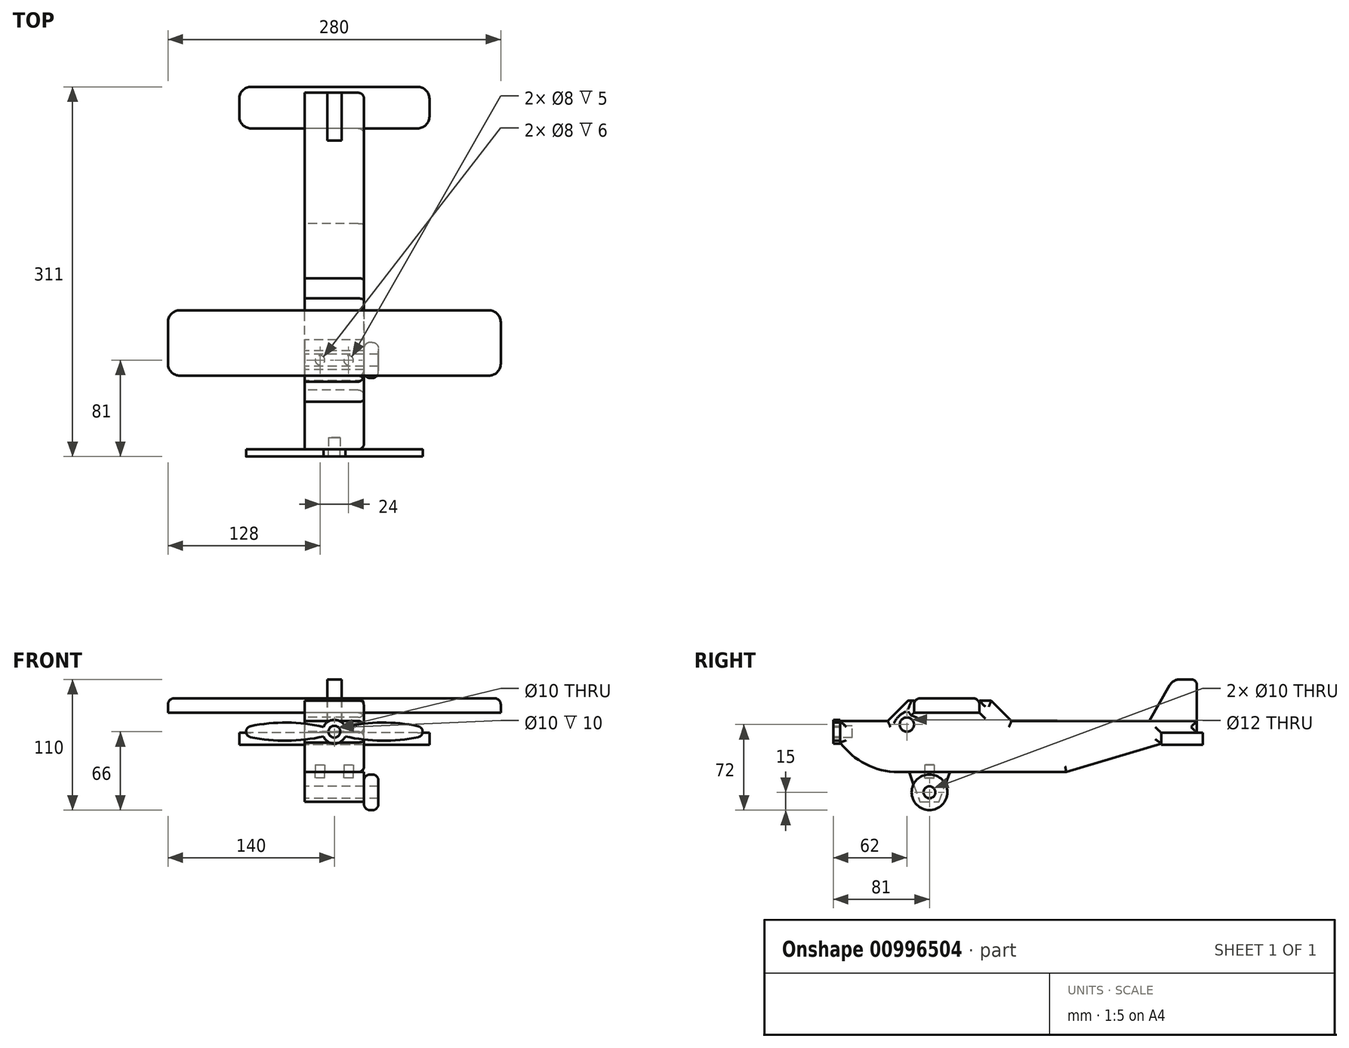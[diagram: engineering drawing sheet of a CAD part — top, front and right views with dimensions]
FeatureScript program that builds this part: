
annotation { "Feature Type Name" : "Feature", "Feature Type Description" : "" }
export const myFeature = defineFeature(function(context is Context, id is Id, definition is map)
    precondition{}
    {
        {
            var Q0;
            Q0=qCreatedBy(makeId("Right.planeOp"),FACE);
            var sketch = newSketch(context, id + "F0", { "sketchPlane" : qUnion([Q0])});
            skLineSegment(sketch, "E0", {"start": v(-150, 0) * mm, "end": v(-150, 18) * mm});
            skLineSegment(sketch, "E1", {"start": v(-150, 18) * mm, "end": v(-110, 18) * mm});
            skLineSegment(sketch, "E2", {"start": v(-110, 18) * mm, "end": v(-93, 35) * mm});
            skLineSegment(sketch, "E3", {"start": v(-93, 35) * mm, "end": v(-88, 35) * mm});
            skLineSegment(sketch, "E4", {"start": v(-88, 35) * mm, "end": v(-88, 25) * mm});
            skLineSegment(sketch, "E5", {"start": v(-88, 25) * mm, "end": v(-33, 25) * mm});
            skLineSegment(sketch, "E6", {"start": v(-33, 25) * mm, "end": v(-33, 35) * mm});
            skLineSegment(sketch, "E7", {"start": v(-33, 35) * mm, "end": v(-23, 35) * mm});
            skLineSegment(sketch, "E8", {"start": v(-23, 35) * mm, "end": v(-6, 18) * mm});
            skLineSegment(sketch, "E9", {"start": v(-6, 18) * mm, "end": v(150, 18) * mm});
            skLineSegment(sketch, "E10", {"start": v(150, 18) * mm, "end": v(150, 8) * mm});
            skLineSegment(sketch, "E11", {"start": v(120, -1) * mm, "end": v(40, -25) * mm});
            skLineSegment(sketch, "E12", {"start": v(40, -25) * mm, "end": v(-101.27, -25) * mm});
            skArc(sketch, "E13", {"start": v(-150, 0) * mm, "mid": v(-128.65, -18.39) * mm, "end": v(-101.27, -25) * mm});
            skCircle(sketch, "E14", {"center": v(-94, 15) * mm, "radius": 6 * mm});
            skLineSegment(sketch, "E15", {"start": v(120, -1) * mm, "end": v(120, 8) * mm});
            skLineSegment(sketch, "E16", {"start": v(120, 8) * mm, "end": v(150, 8) * mm});
            skSolve(sketch);
        }
        {
            var Q0;
            Q0 = qSketchRegion(id + "F0", true);
            extrude(context, id + "F1", {"entities" : qUnion([Q0]), "depth" : 25 * mm, "offsetDistance" : 25 * mm, "hasSecondDirection" : true, "secondDirectionOppositeDirection" : true, "secondDirectionDepth" : 25 * mm});
        }
        {
            var Q0;
            Q0=qCreatedBy(makeId("Right.planeOp"),FACE);
            var sketch = newSketch(context, id + "F2", { "sketchPlane" : qUnion([Q0])});
            skLineSegment(sketch, "E17.bottom", {"start": v(-88, 25) * mm, "end": v(-33, 25) * mm});
            skLineSegment(sketch, "E17.top", {"start": v(-88, 37) * mm, "end": v(-33, 37) * mm});
            skLineSegment(sketch, "E17.left", {"start": v(-88, 25) * mm, "end": v(-88, 37) * mm});
            skLineSegment(sketch, "E17.right", {"start": v(-33, 25) * mm, "end": v(-33, 37) * mm});
            skSolve(sketch);
        }
        {
            var Q0;
            Q0 = qSketchRegion(id + "F2", true);
            extrude(context, id + "F3", {"entities" : qUnion([Q0]), "depth" : 140 * mm, "offsetDistance" : 25 * mm, "hasSecondDirection" : true, "secondDirectionOppositeDirection" : true, "secondDirectionDepth" : 140 * mm});
        }
        {
            var Q0;
            Q0=makeQuery(id+"F3.opExtrude","CAP_EDGE",EDGE,{"disambiguationData":[OSD([sQuery(id+"F2.wireOp",EDGE,"E17.left")])],"isStart":false});
            var Q1;
            Q1=makeQuery(id+"F3.opExtrude","CAP_EDGE",EDGE,{"disambiguationData":[OSD([sQuery(id+"F2.wireOp",EDGE,"E17.right")])],"isStart":false});
            var Q2;
            Q2=makeQuery(id+"F3.opExtrude","CAP_EDGE",EDGE,{"disambiguationData":[OSD([sQuery(id+"F2.wireOp",EDGE,"E17.left")])],"isStart":true});
            var Q3;
            Q3=makeQuery(id+"F3.opExtrude","CAP_EDGE",EDGE,{"disambiguationData":[OSD([sQuery(id+"F2.wireOp",EDGE,"E17.right")])],"isStart":true});
            fillet(context, id + "F4", {"entities" : qUnion([Q0, Q1, Q2, Q3]), "radius" : 10 * mm, "tangentPropagation" : true, "allowEdgeOverflow" : false});
        }
        {
            var Q0;
            Q0=makeQuery(id+"F3.opExtrude","SWEPT_FACE",FACE,{"disambiguationData":[OSD([sQuery(id+"F2.wireOp",EDGE,"E17.top")])]});
            fillet(context, id + "F5", {"entities" : qUnion([Q0]), "radius" : 5 * mm, "tangentPropagation" : true, "allowEdgeOverflow" : false});
        }
        {
            var Q0;
            Q0=qCreatedBy(makeId("Right.planeOp"),FACE);
            var sketch = newSketch(context, id + "F6", { "sketchPlane" : qUnion([Q0])});
            skLineSegment(sketch, "E18.bottom", {"start": v(120, 8) * mm, "end": v(155, 8) * mm});
            skLineSegment(sketch, "E18.top", {"start": v(120, -2) * mm, "end": v(155, -2) * mm});
            skLineSegment(sketch, "E18.left", {"start": v(120, 8) * mm, "end": v(120, -2) * mm});
            skLineSegment(sketch, "E18.right", {"start": v(155, 8) * mm, "end": v(155, -2) * mm});
            skSolve(sketch);
        }
        {
            var Q0;
            Q0 = qSketchRegion(id + "F6", true);
            extrude(context, id + "F7", {"entities" : qUnion([Q0]), "depth" : 80 * mm, "offsetDistance" : 25 * mm, "hasSecondDirection" : true, "secondDirectionOppositeDirection" : true, "secondDirectionDepth" : 80 * mm});
        }
        {
            var Q0;
            Q0=makeQuery(id+"F7.opExtrude","CAP_EDGE",EDGE,{"disambiguationData":[OSD([sQuery(id+"F6.wireOp",EDGE,"E18.left")])],"isStart":false});
            var Q1;
            Q1=makeQuery(id+"F7.opExtrude","CAP_EDGE",EDGE,{"disambiguationData":[OSD([sQuery(id+"F6.wireOp",EDGE,"E18.right")])],"isStart":false});
            var Q2;
            Q2=makeQuery(id+"F7.opExtrude","CAP_EDGE",EDGE,{"disambiguationData":[OSD([sQuery(id+"F6.wireOp",EDGE,"E18.right")])],"isStart":true});
            var Q3;
            Q3=makeQuery(id+"F7.opExtrude","CAP_EDGE",EDGE,{"disambiguationData":[OSD([sQuery(id+"F6.wireOp",EDGE,"E18.left")])],"isStart":true});
            fillet(context, id + "F8", {"entities" : qUnion([Q0, Q1, Q2, Q3]), "radius" : 10 * mm, "tangentPropagation" : true, "allowEdgeOverflow" : false});
        }
        {
            var Q0;
            Q0=qCreatedBy(makeId("Right.planeOp"),FACE);
            var sketch = newSketch(context, id + "F9", { "sketchPlane" : qUnion([Q0])});
            skLineSegment(sketch, "E19.0", {"start": v(-6, 18) * mm, "end": v(150, 18) * mm});
            skLineSegment(sketch, "E20.0", {"start": v(109.8, 18) * mm, "end": v(150, 18) * mm});
            skLineSegment(sketch, "E21", {"start": v(150, 18) * mm, "end": v(150, 53) * mm});
            skLineSegment(sketch, "E22", {"start": v(150, 53) * mm, "end": v(130, 53) * mm});
            skLineSegment(sketch, "E23", {"start": v(130, 53) * mm, "end": v(109.8, 18) * mm});
            skSolve(sketch);
        }
        {
            var Q0;
            Q0 = qSketchRegion(id + "F9", true);
            extrude(context, id + "F10", {"entities" : qUnion([Q0]), "depth" : 6 * mm, "offsetDistance" : 25 * mm, "hasSecondDirection" : true, "secondDirectionOppositeDirection" : true, "secondDirectionDepth" : 6 * mm});
        }
        {
            var Q0;
            Q0=makeQuery(id+"F10.opExtrude","SWEPT_EDGE",EDGE,{"disambiguationData":[OSD([sQuery(id+"F9.wireOp",EDGE,"E22"),sQuery(id+"F9.wireOp",EDGE,"E23")])]});
            fillet(context, id + "F11", {"entities" : qUnion([Q0]), "radius" : 10 * mm, "tangentPropagation" : true, "allowEdgeOverflow" : false});
        }
        {
            var Q0;
            Q0=makeQuery(id+"F10.opExtrude","SWEPT_EDGE",EDGE,{"disambiguationData":[OSD([sQuery(id+"F9.wireOp",EDGE,"E21"),sQuery(id+"F9.wireOp",EDGE,"E22")])]});
            fillet(context, id + "F12", {"entities" : qUnion([Q0]), "radius" : 5 * mm, "tangentPropagation" : true, "allowEdgeOverflow" : false});
        }
        {
            var Q0;
            Q0=qCreatedBy(makeId("Right.planeOp"),FACE);
            var sketch = newSketch(context, id + "F13", { "sketchPlane" : qUnion([Q0])});
            skLineSegment(sketch, "E24.0", {"start": v(-57.9, -25) * mm, "end": v(-92.1, -25) * mm});
            skLineSegment(sketch, "E25", {"start": v(-92.1, -25) * mm, "end": v(-83, -50) * mm});
            skLineSegment(sketch, "E26", {"start": v(-83, -50) * mm, "end": v(-67, -50) * mm});
            skLineSegment(sketch, "E27", {"start": v(-67, -50) * mm, "end": v(-57.9, -25) * mm});
            skCircle(sketch, "E28", {"center": v(-75, -42) * mm, "radius": 5 * mm});
            skPoint(sketch, "E28.centerSnap0", {"position": v(-75, -50) * mm});
            skPoint(sketch, "E29.orphan", {"position": v(-101.27, -25) * mm});
            skPoint(sketch, "E30.orphan", {"position": v(40, -25) * mm});
            skSolve(sketch);
        }
        {
            var Q0;
            Q0 = qSketchRegion(id + "F13", true);
            var Q1;
            Q1=makeQuery(id+"F1.opExtrude","CAP_FACE",FACE,{"disambiguationData":[OSD([sQuery(id+"F0.wireOp",EDGE,"E0"),sQuery(id+"F0.wireOp",EDGE,"E1"),sQuery(id+"F0.wireOp",EDGE,"E2"),sQuery(id+"F0.wireOp",EDGE,"E3"),sQuery(id+"F0.wireOp",EDGE,"E4"),sQuery(id+"F0.wireOp",EDGE,"E5"),sQuery(id+"F0.wireOp",EDGE,"E6"),sQuery(id+"F0.wireOp",EDGE,"E7"),sQuery(id+"F0.wireOp",EDGE,"E8"),sQuery(id+"F0.wireOp",EDGE,"E9"),sQuery(id+"F0.wireOp",EDGE,"E10"),sQuery(id+"F0.wireOp",EDGE,"E11"),sQuery(id+"F0.wireOp",EDGE,"E12"),sQuery(id+"F0.wireOp",EDGE,"E13"),sQuery(id+"F0.wireOp",EDGE,"E14"),sQuery(id+"F0.wireOp",EDGE,"E15"),sQuery(id+"F0.wireOp",EDGE,"E16")])],"isStart":false});
            var Q2;
            Q2=makeQuery(id+"F1.opExtrude","CAP_FACE",FACE,{"disambiguationData":[OSD([sQuery(id+"F0.wireOp",EDGE,"E0"),sQuery(id+"F0.wireOp",EDGE,"E1"),sQuery(id+"F0.wireOp",EDGE,"E2"),sQuery(id+"F0.wireOp",EDGE,"E3"),sQuery(id+"F0.wireOp",EDGE,"E4"),sQuery(id+"F0.wireOp",EDGE,"E5"),sQuery(id+"F0.wireOp",EDGE,"E6"),sQuery(id+"F0.wireOp",EDGE,"E7"),sQuery(id+"F0.wireOp",EDGE,"E8"),sQuery(id+"F0.wireOp",EDGE,"E9"),sQuery(id+"F0.wireOp",EDGE,"E10"),sQuery(id+"F0.wireOp",EDGE,"E11"),sQuery(id+"F0.wireOp",EDGE,"E12"),sQuery(id+"F0.wireOp",EDGE,"E13"),sQuery(id+"F0.wireOp",EDGE,"E14"),sQuery(id+"F0.wireOp",EDGE,"E15"),sQuery(id+"F0.wireOp",EDGE,"E16")])],"isStart":true});
            extrude(context, id + "F14", {"entities" : qUnion([Q0]), "endBound" : BoundingType.UP_TO_SURFACE, "depth" : 25 * mm, "endBoundEntityFace" : qUnion([Q1]), "offsetDistance" : 25 * mm, "hasSecondDirection" : true, "secondDirectionBound" : SecondDirectionBoundingType.UP_TO_SURFACE, "secondDirectionOppositeDirection" : true, "secondDirectionDepth" : 25 * mm, "secondDirectionBoundEntityFace" : qUnion([Q2])});
        }
        {
            var Q0;
            Q0=makeQuery(id+"F14.opExtrude","CAP_FACE",FACE,{"disambiguationData":[OSD([sQuery(id+"F13.wireOp",EDGE,"E24.0"),sQuery(id+"F13.wireOp",EDGE,"E25"),sQuery(id+"F13.wireOp",EDGE,"E26"),sQuery(id+"F13.wireOp",EDGE,"E27"),sQuery(id+"F13.wireOp",EDGE,"E28")])],"isStart":false});
            var sketch = newSketch(context, id + "F15", { "sketchPlane" : qUnion([Q0])});
            skCircle(sketch, "E31.0", {"center": v(-75, -42) * mm, "radius": 5 * mm});
            skCircle(sketch, "E32", {"center": v(-75, -42) * mm, "radius": 15 * mm});
            skSolve(sketch);
        }
        {
            var Q0;
            Q0 = qSketchRegion(id + "F15", true);
            extrude(context, id + "F16", {"entities" : qUnion([Q0]), "depth" : 12 * mm, "offsetDistance" : 25 * mm});
        }
        {
            var Q0;
            Q0=makeQuery(id+"F16.opExtrude","SWEPT_FACE",FACE,{"disambiguationData":[OSD([sQuery(id+"F15.wireOp",EDGE,"E32")])]});
            fillet(context, id + "F17", {"entities" : qUnion([Q0]), "radius" : 5 * mm, "tangentPropagation" : true, "allowEdgeOverflow" : false});
        }
        {
            var Q0;
            Q0=makeQuery(id+"F1.opExtrude","SWEPT_FACE",FACE,{"disambiguationData":[OSD([sQuery(id+"F0.wireOp",EDGE,"E0")])]});
            var sketch = newSketch(context, id + "F18", { "sketchPlane" : qUnion([Q0])});
            skCircle(sketch, "E33", {"center": v(0, 9) * mm, "radius": 5 * mm});
            skPoint(sketch, "E33.centerSnap0", {"position": v(25, 9) * mm});
            skPoint(sketch, "E33.centerSnap1", {"position": v(0, 18) * mm});
            skSolve(sketch);
        }
        {
            var Q0;
            Q0 = qSketchRegion(id + "F18", true);
            extrude(context, id + "F19", {"entities" : qUnion([Q0]), "operationType" : NewBodyOperationType.REMOVE, "oppositeDirection" : true, "depth" : 10 * mm, "offsetDistance" : 25 * mm});
        }
        {
            var Q0;
            Q0=makeQuery(id+"F1.opExtrude","SWEPT_FACE",FACE,{"disambiguationData":[OSD([sQuery(id+"F0.wireOp",EDGE,"E0")])]});
            var sketch = newSketch(context, id + "F20", { "sketchPlane" : qUnion([Q0])});
            skCircle(sketch, "E34.0", {"center": v(0, 9) * mm, "radius": 5 * mm});
            skArc(sketch, "E35", {"start": v(9.2, 12.9) * mm, "mid": v(5.52, 17.34) * mm, "end": v(0, 19) * mm});
            skLineSegment(sketch, "E36", {"start": v(-10, 9) * mm, "end": v(97.07, 9) * mm, "construction": true});
            skArc(sketch, "E37", {"start": v(70.54, 13.6) * mm, "mid": v(39.83, 16.65) * mm, "end": v(9.2, 12.9) * mm});
            skArc(sketch, "E38", {"start": v(74.27, 9) * mm, "mid": v(73.22, 11.96) * mm, "end": v(70.54, 13.6) * mm});
            skArc(sketch, "E39.MirrorCS", {"start": v(74.27, 9) * mm, "mid": v(73.22, 6.04) * mm, "end": v(70.54, 4.4) * mm});
            skArc(sketch, "E40.MirrorCS", {"start": v(9.2, 5.1) * mm, "mid": v(5.52, 0.66) * mm, "end": v(0, -1) * mm});
            skArc(sketch, "E41.MirrorCS", {"start": v(70.54, 4.4) * mm, "mid": v(39.83, 1.35) * mm, "end": v(9.2, 5.1) * mm});
            skLineSegment(sketch, "E42", {"start": v(0, -1) * mm, "end": v(0, 60.72) * mm, "construction": true});
            skPoint(sketch, "E43.orphan", {"position": v(-10, 9) * mm});
            skArc(sketch, "E44.MirrorCS", {"start": v(-74.27, 9) * mm, "mid": v(-73.22, 11.96) * mm, "end": v(-70.54, 13.6) * mm});
            skArc(sketch, "E45.MirrorCS", {"start": v(-74.27, 9) * mm, "mid": v(-73.22, 6.04) * mm, "end": v(-70.54, 4.4) * mm});
            skArc(sketch, "E46.MirrorCS", {"start": v(-9.2, 5.1) * mm, "mid": v(-5.52, 0.66) * mm, "end": v(0, -1) * mm});
            skArc(sketch, "E47.MirrorCS", {"start": v(-9.2, 12.9) * mm, "mid": v(-5.52, 17.34) * mm, "end": v(0, 19) * mm});
            skPoint(sketch, "E48.MirrorP", {"position": v(10, 9) * mm});
            skArc(sketch, "E49.MirrorCS", {"start": v(-70.54, 13.6) * mm, "mid": v(-39.83, 16.65) * mm, "end": v(-9.2, 12.9) * mm});
            skArc(sketch, "E50.MirrorCS", {"start": v(-70.54, 4.4) * mm, "mid": v(-39.83, 1.35) * mm, "end": v(-9.2, 5.1) * mm});
            skSolve(sketch);
        }
        {
            var Q0;
            Q0 = qSketchRegion(id + "F20", true);
            extrude(context, id + "F21", {"entities" : qUnion([Q0]), "depth" : 6 * mm, "offsetDistance" : 25 * mm});
        }
        {
            var Q0;
            Q0=makeQuery(id+"F14.opExtrude","SWEPT_FACE",FACE,{"disambiguationData":[OSD([sQuery(id+"F13.wireOp",EDGE,"E24.0")])]});
            var sketch = newSketch(context, id + "F22", { "sketchPlane" : qUnion([Q0])});
            skCircle(sketch, "E51", {"center": v(-12, -75) * mm, "radius": 4 * mm});
            skPoint(sketch, "E51.centerSnap0", {"position": v(-25, -75) * mm});
            skCircle(sketch, "E52", {"center": v(12, -75) * mm, "radius": 4 * mm});
            skSolve(sketch);
        }
        {
            var Q0;
            Q0 = qSketchRegion(id + "F22", true);
            extrude(context, id + "F23", {"entities" : qUnion([Q0]), "operationType" : NewBodyOperationType.REMOVE, "oppositeDirection" : true, "depth" : 5 * mm, "offsetDistance" : 25 * mm});
        }
        {
            var Q0;
            Q0=makeQuery(id+"F1.opExtrude","SWEPT_FACE",FACE,{"disambiguationData":[OSD([sQuery(id+"F0.wireOp",EDGE,"E12")])]});
            var sketch = newSketch(context, id + "F24", { "sketchPlane" : qUnion([Q0])});
            skCircle(sketch, "E53.0", {"center": v(-12, 75) * mm, "radius": 4 * mm});
            skCircle(sketch, "E54.0", {"center": v(12, 75) * mm, "radius": 4 * mm});
            skSolve(sketch);
        }
        {
            var Q0;
            Q0 = qSketchRegion(id + "F24", true);
            extrude(context, id + "F25", {"entities" : qUnion([Q0]), "operationType" : NewBodyOperationType.REMOVE, "oppositeDirection" : true, "depth" : 6 * mm, "offsetDistance" : 25 * mm});
        }
        {
            var Q0;
            Q0=makeQuery(id+"F1.opExtrude","CAP_FACE",FACE,{"disambiguationData":[OSD([sQuery(id+"F0.wireOp",EDGE,"E0"),sQuery(id+"F0.wireOp",EDGE,"E1"),sQuery(id+"F0.wireOp",EDGE,"E2"),sQuery(id+"F0.wireOp",EDGE,"E3"),sQuery(id+"F0.wireOp",EDGE,"E4"),sQuery(id+"F0.wireOp",EDGE,"E5"),sQuery(id+"F0.wireOp",EDGE,"E6"),sQuery(id+"F0.wireOp",EDGE,"E7"),sQuery(id+"F0.wireOp",EDGE,"E8"),sQuery(id+"F0.wireOp",EDGE,"E9"),sQuery(id+"F0.wireOp",EDGE,"E10"),sQuery(id+"F0.wireOp",EDGE,"E11"),sQuery(id+"F0.wireOp",EDGE,"E12"),sQuery(id+"F0.wireOp",EDGE,"E13"),sQuery(id+"F0.wireOp",EDGE,"E14"),sQuery(id+"F0.wireOp",EDGE,"E15"),sQuery(id+"F0.wireOp",EDGE,"E16")])],"isStart":false});
            fillet(context, id + "F26", {"entities" : qUnion([Q0]), "tangentPropagation" : true, "radius" : 5 * mm, "defaultsChanged" : false, "vertexSettings" : [], "allowEdgeOverflow" : false});
        }
    });
